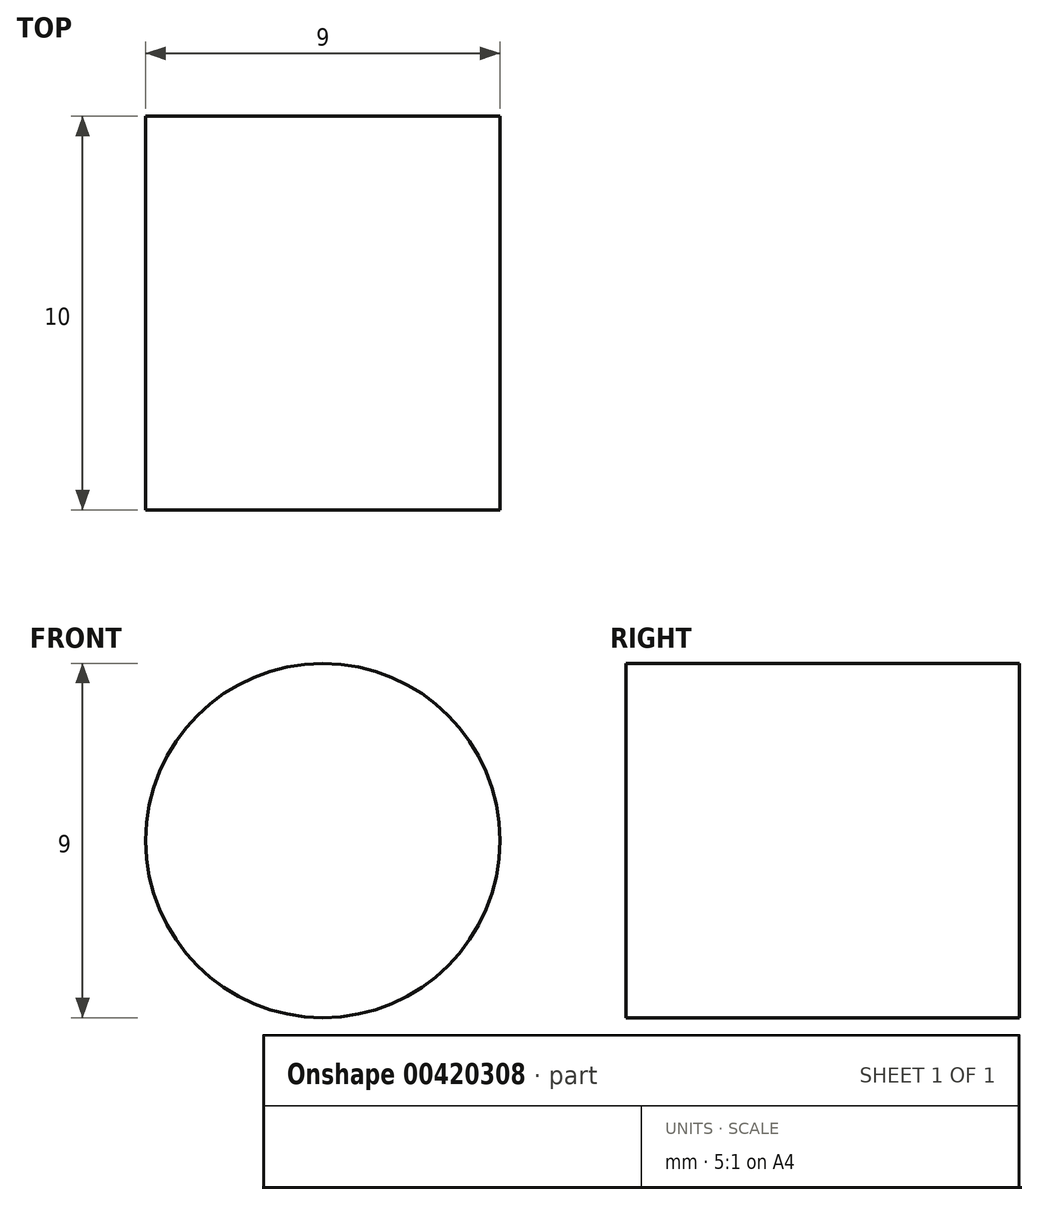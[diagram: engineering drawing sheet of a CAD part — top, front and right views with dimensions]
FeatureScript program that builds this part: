
annotation { "Feature Type Name" : "Feature", "Feature Type Description" : "" }
export const myFeature = defineFeature(function(context is Context, id is Id, definition is map)
    precondition{}
    {
        {
            var Q0;
            Q0=qCreatedBy(makeId("Front.planeOp"),FACE);
            var sketch = newSketch(context, id + "F0", { "sketchPlane" : qUnion([Q0])});
            skCircle(sketch, "E0", {"center": v(0, 0) * mm, "radius": 4.5 * mm});
            skSolve(sketch);
        }
        {
            var Q0;
            Q0=makeQuery(id+"F0.imprint","IMPRINT",FACE,{"disambiguationData":[TD([[makeQuery(id+"F0.imprint","IMPRINT",EDGE,{"derivedFrom":sQuery(id+"F0.wireOp",EDGE,"E0")}),1.0]])]});
            extrude(context, id + "F1", {"entities" : qUnion([Q0]), "depth" : 10 * mm, "offsetDistance" : 25 * mm});
        }
    });
